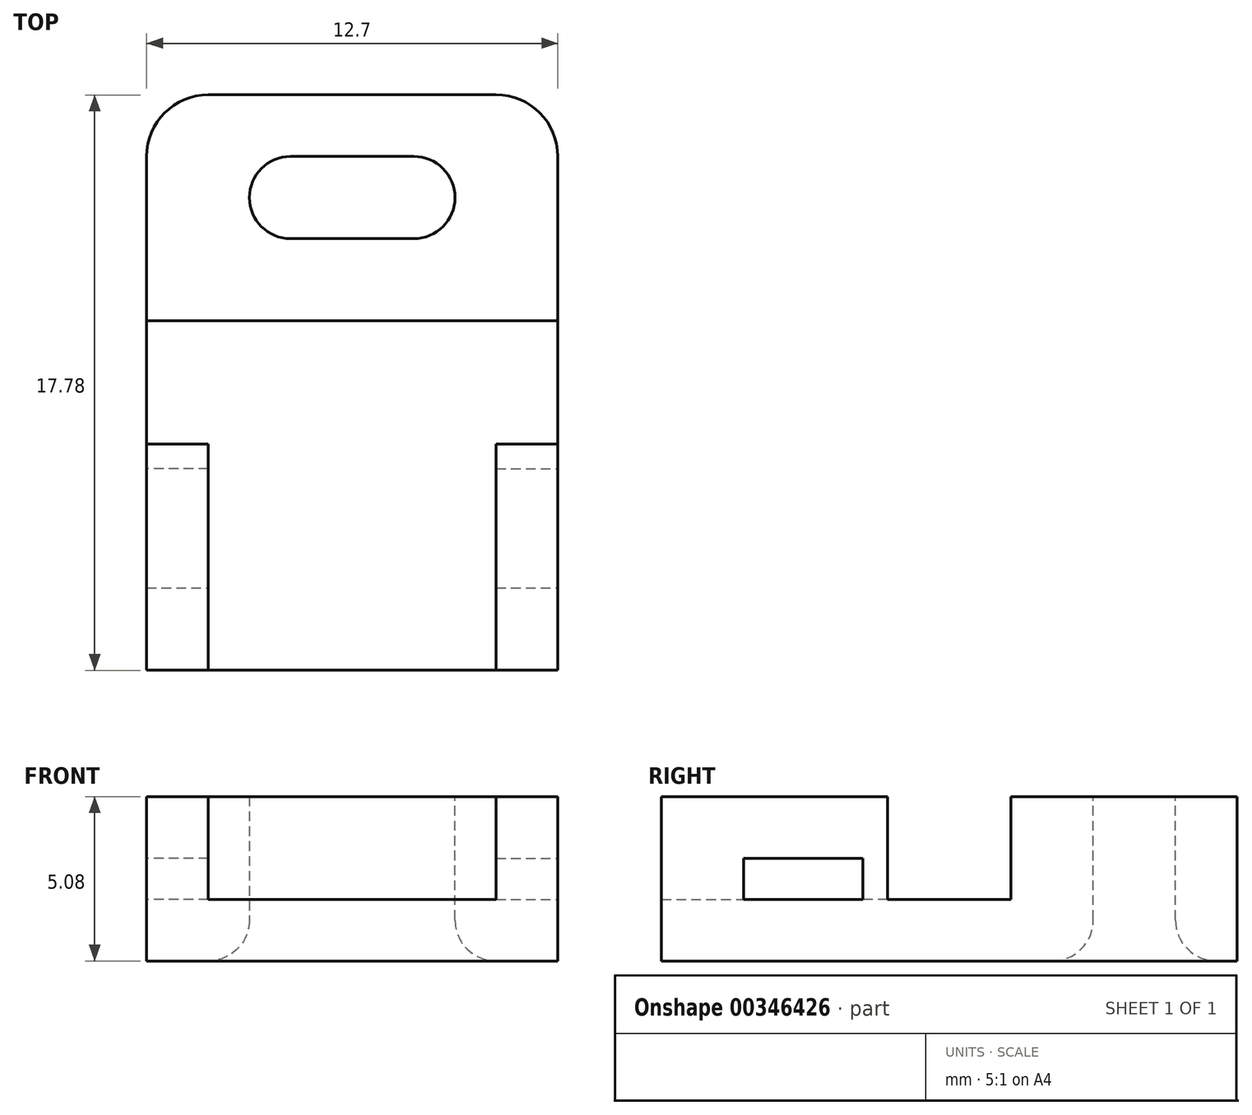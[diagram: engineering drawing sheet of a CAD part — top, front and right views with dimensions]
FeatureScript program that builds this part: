
annotation { "Feature Type Name" : "Feature", "Feature Type Description" : "" }
export const myFeature = defineFeature(function(context is Context, id is Id, definition is map)
    precondition{}
    {
        {
            var Q0;
            Q0=qCreatedBy(makeId("Top.planeOp"),FACE);
            var sketch = newSketch(context, id + "F0", { "sketchPlane" : qUnion([Q0])});
            skLineSegment(sketch, "E0.bottom", {"start": v(-27.07, 22.58) * mm, "end": v(-14.37, 22.58) * mm});
            skLineSegment(sketch, "E0.top", {"start": v(-27.07, 7.34) * mm, "end": v(-14.37, 7.34) * mm});
            skLineSegment(sketch, "E0.left", {"start": v(-27.07, 22.58) * mm, "end": v(-27.07, 7.34) * mm});
            skLineSegment(sketch, "E0.right", {"start": v(-14.37, 22.58) * mm, "end": v(-14.37, 7.34) * mm});
            skSolve(sketch);
        }
        {
            var Q0;
            Q0=makeQuery(id+"F0.imprint","IMPRINT",FACE,{"disambiguationData":[TD([[makeQuery(id+"F0.imprint","IMPRINT",EDGE,{"derivedFrom":sQuery(id+"F0.wireOp",EDGE,"E0.bottom")}),-1.0]])]});
            extrude(context, id + "F1", {"entities" : qUnion([Q0]), "depth" : 5.08 * mm});
        }
        {
            var Q0;
            Q0=makeQuery(id+"F1.opExtrude","CAP_FACE",FACE,{"disambiguationData":[OSD([sQuery(id+"F0.wireOp",EDGE,"E0.bottom"),sQuery(id+"F0.wireOp",EDGE,"E0.top"),sQuery(id+"F0.wireOp",EDGE,"E0.left"),sQuery(id+"F0.wireOp",EDGE,"E0.right")])],"isStart":false});
            var sketch = newSketch(context, id + "F2", { "sketchPlane" : qUnion([Q0])});
            skLineSegment(sketch, "E1.bottom", {"start": v(-23.9, 20.68) * mm, "end": v(-17.55, 20.68) * mm});
            skLineSegment(sketch, "E1.top", {"start": v(-23.9, 18.14) * mm, "end": v(-17.55, 18.14) * mm});
            skLineSegment(sketch, "E1.left", {"start": v(-23.9, 20.68) * mm, "end": v(-23.9, 18.14) * mm});
            skLineSegment(sketch, "E1.right", {"start": v(-17.55, 20.68) * mm, "end": v(-17.55, 18.14) * mm});
            skPoint(sketch, "E1.middle", {"position": v(-20.72, 19.4) * mm});
            skPoint(sketch, "E1.middle.positionSnap0", {"position": v(-20.72, 22.58) * mm});
            skPoint(sketch, "E1.centerSnap0", {"position": v(-20.72, 22.58) * mm});
            skSolve(sketch);
        }
        {
            var Q0;
            Q0=makeQuery(id+"F2.imprint","IMPRINT",FACE,{"disambiguationData":[TD([[makeQuery(id+"F2.imprint","IMPRINT",EDGE,{"derivedFrom":sQuery(id+"F2.wireOp",EDGE,"E1.bottom")}),-1.0]])]});
            extrude(context, id + "F3", {"entities" : qUnion([Q0]), "operationType" : NewBodyOperationType.REMOVE, "oppositeDirection" : true, "depth" : 25.4 * mm});
        }
        {
            var Q0;
            Q0=makeQuery(id+"F3.boolean.opBoolean","COPY",EDGE,{"derivedFrom":makeQuery(id+"F3.opExtrude","CAP_EDGE",EDGE,{"disambiguationData":[OSD([sQuery(id+"F2.wireOp",EDGE,"E1.top")])],"isStart":true})});
            var Q1;
            Q1=makeQuery(id+"F3.boolean.opBoolean","COPY",EDGE,{"derivedFrom":makeQuery(id+"F3.opExtrude","CAP_EDGE",EDGE,{"disambiguationData":[OSD([sQuery(id+"F2.wireOp",EDGE,"E1.right")])],"isStart":true})});
            var Q2;
            Q2=makeQuery(id+"F3.boolean.opBoolean","COPY",EDGE,{"derivedFrom":makeQuery(id+"F3.opExtrude","CAP_EDGE",EDGE,{"disambiguationData":[OSD([sQuery(id+"F2.wireOp",EDGE,"E1.left")])],"isStart":true})});
            var Q3;
            Q3=makeQuery(id+"F3.boolean.opBoolean","COPY",EDGE,{"derivedFrom":makeQuery(id+"F3.opExtrude","CAP_EDGE",EDGE,{"disambiguationData":[OSD([sQuery(id+"F2.wireOp",EDGE,"E1.bottom")])],"isStart":true})});
            var Q4;
            Q4=makeQuery(id+"F3.boolean.opBoolean","INTERSECT",EDGE,{"derivedFrom":[makeQuery(id+"F1.opExtrude","CAP_FACE",FACE,{"disambiguationData":[OSD([sQuery(id+"F0.wireOp",EDGE,"E0.bottom"),sQuery(id+"F0.wireOp",EDGE,"E0.top"),sQuery(id+"F0.wireOp",EDGE,"E0.left"),sQuery(id+"F0.wireOp",EDGE,"E0.right")])],"isStart":true}),makeQuery(id+"F3.opExtrude","SWEPT_FACE",FACE,{"disambiguationData":[OSD([sQuery(id+"F2.wireOp",EDGE,"E1.right")])]})]});
            var Q5;
            Q5=makeQuery(id+"F3.boolean.opBoolean","INTERSECT",EDGE,{"derivedFrom":[makeQuery(id+"F1.opExtrude","CAP_FACE",FACE,{"disambiguationData":[OSD([sQuery(id+"F0.wireOp",EDGE,"E0.bottom"),sQuery(id+"F0.wireOp",EDGE,"E0.top"),sQuery(id+"F0.wireOp",EDGE,"E0.left"),sQuery(id+"F0.wireOp",EDGE,"E0.right")])],"isStart":true}),makeQuery(id+"F3.opExtrude","SWEPT_FACE",FACE,{"disambiguationData":[OSD([sQuery(id+"F2.wireOp",EDGE,"E1.top")])]})]});
            var Q6;
            Q6=makeQuery(id+"F3.boolean.opBoolean","INTERSECT",EDGE,{"derivedFrom":[makeQuery(id+"F1.opExtrude","CAP_FACE",FACE,{"disambiguationData":[OSD([sQuery(id+"F0.wireOp",EDGE,"E0.bottom"),sQuery(id+"F0.wireOp",EDGE,"E0.top"),sQuery(id+"F0.wireOp",EDGE,"E0.left"),sQuery(id+"F0.wireOp",EDGE,"E0.right")])],"isStart":true}),makeQuery(id+"F3.opExtrude","SWEPT_FACE",FACE,{"disambiguationData":[OSD([sQuery(id+"F2.wireOp",EDGE,"E1.left")])]})]});
            var Q7;
            Q7=makeQuery(id+"F3.boolean.opBoolean","INTERSECT",EDGE,{"derivedFrom":[makeQuery(id+"F1.opExtrude","CAP_FACE",FACE,{"disambiguationData":[OSD([sQuery(id+"F0.wireOp",EDGE,"E0.bottom"),sQuery(id+"F0.wireOp",EDGE,"E0.top"),sQuery(id+"F0.wireOp",EDGE,"E0.left"),sQuery(id+"F0.wireOp",EDGE,"E0.right")])],"isStart":true}),makeQuery(id+"F3.opExtrude","SWEPT_FACE",FACE,{"disambiguationData":[OSD([sQuery(id+"F2.wireOp",EDGE,"E1.bottom")])]})]});
            var Q8;
            Q8=makeQuery(id+"F3.boolean.opBoolean","COPY",EDGE,{"derivedFrom":makeQuery(id+"F3.opExtrude","SWEPT_EDGE",EDGE,{"disambiguationData":[OSD([sQuery(id+"F2.wireOp",EDGE,"E1.top"),sQuery(id+"F2.wireOp",EDGE,"E1.right")])]})});
            var Q9;
            Q9=makeQuery(id+"F3.boolean.opBoolean","COPY",EDGE,{"derivedFrom":makeQuery(id+"F3.opExtrude","SWEPT_EDGE",EDGE,{"disambiguationData":[OSD([sQuery(id+"F2.wireOp",EDGE,"E1.top"),sQuery(id+"F2.wireOp",EDGE,"E1.left")])]})});
            var Q10;
            Q10=makeQuery(id+"F3.boolean.opBoolean","COPY",EDGE,{"derivedFrom":makeQuery(id+"F3.opExtrude","SWEPT_EDGE",EDGE,{"disambiguationData":[OSD([sQuery(id+"F2.wireOp",EDGE,"E1.bottom"),sQuery(id+"F2.wireOp",EDGE,"E1.left")])]})});
            var Q11;
            Q11=makeQuery(id+"F3.boolean.opBoolean","COPY",EDGE,{"derivedFrom":makeQuery(id+"F3.opExtrude","SWEPT_EDGE",EDGE,{"disambiguationData":[OSD([sQuery(id+"F2.wireOp",EDGE,"E1.bottom"),sQuery(id+"F2.wireOp",EDGE,"E1.right")])]})});
            fillet(context, id + "F4", {"entities" : qUnion([Q0, Q1, Q2, Q3, Q4, Q5, Q6, Q7, Q8, Q9, Q10, Q11]), "radius" : 1.27 * mm, "tangentPropagation" : true, "allowEdgeOverflow" : false});
        }
        {
            var Q0;
            Q0=makeQuery(id+"F1.opExtrude","SWEPT_EDGE",EDGE,{"disambiguationData":[OSD([sQuery(id+"F0.wireOp",EDGE,"E0.bottom"),sQuery(id+"F0.wireOp",EDGE,"E0.left")])]});
            var Q1;
            Q1=makeQuery(id+"F1.opExtrude","SWEPT_EDGE",EDGE,{"disambiguationData":[OSD([sQuery(id+"F0.wireOp",EDGE,"E0.bottom"),sQuery(id+"F0.wireOp",EDGE,"E0.right")])]});
            fillet(context, id + "F5", {"entities" : qUnion([Q0, Q1]), "radius" : 1.9 * mm, "tangentPropagation" : true, "allowEdgeOverflow" : false});
        }
        {
            var Q0;
            Q0=makeQuery(id+"F1.opExtrude","SWEPT_FACE",FACE,{"disambiguationData":[OSD([sQuery(id+"F0.wireOp",EDGE,"E0.right")])]});
            var sketch = newSketch(context, id + "F6", { "sketchPlane" : qUnion([Q0])});
            skLineSegment(sketch, "E2.bottom", {"start": v(9.88, 3.17) * mm, "end": v(15.6, 3.17) * mm});
            skLineSegment(sketch, "E2.top", {"start": v(9.88, 1.9) * mm, "end": v(15.6, 1.9) * mm});
            skLineSegment(sketch, "E2.left", {"start": v(9.88, 3.17) * mm, "end": v(9.88, 1.9) * mm});
            skLineSegment(sketch, "E2.right", {"start": v(15.6, 3.17) * mm, "end": v(15.6, 1.9) * mm});
            skPoint(sketch, "E2.middle", {"position": v(12.74, 2.54) * mm});
            skPoint(sketch, "E2.middle.positionSnap0", {"position": v(7.34, 2.54) * mm});
            skPoint(sketch, "E2.centerSnap0", {"position": v(7.34, 2.54) * mm});
            skSolve(sketch);
        }
        {
            var Q0;
            Q0 = qSketchRegion(id + "F6", true);
            extrude(context, id + "F7", {"entities" : qUnion([Q0]), "operationType" : NewBodyOperationType.REMOVE, "oppositeDirection" : true, "depth" : 25.4 * mm});
        }
        {
            var Q0;
            Q0=makeQuery(id+"F1.opExtrude","CAP_FACE",FACE,{"disambiguationData":[OSD([sQuery(id+"F0.wireOp",EDGE,"E0.bottom"),sQuery(id+"F0.wireOp",EDGE,"E0.top"),sQuery(id+"F0.wireOp",EDGE,"E0.left"),sQuery(id+"F0.wireOp",EDGE,"E0.right")])],"isStart":false});
            var sketch = newSketch(context, id + "F8", { "sketchPlane" : qUnion([Q0])});
            skLineSegment(sketch, "E3.bottom", {"start": v(-25.17, 7.34) * mm, "end": v(-16.28, 7.34) * mm});
            skLineSegment(sketch, "E3.top", {"start": v(-25.17, 15.6) * mm, "end": v(-16.28, 15.6) * mm});
            skLineSegment(sketch, "E3.left", {"start": v(-25.17, 7.34) * mm, "end": v(-25.17, 15.6) * mm});
            skLineSegment(sketch, "E3.right", {"start": v(-16.28, 7.34) * mm, "end": v(-16.28, 15.6) * mm});
            skPoint(sketch, "E3.middle", {"position": v(-20.72, 11.47) * mm});
            skPoint(sketch, "E3.middle.positionSnap0", {"position": v(-20.72, 7.34) * mm});
            skPoint(sketch, "E3.centerSnap0", {"position": v(-20.72, 7.34) * mm});
            skSolve(sketch);
        }
        {
            var Q0;
            Q0 = qSketchRegion(id + "F8", true);
            var Q1;
            Q1=makeQuery(id+"F7.boolean.opBoolean","COPY",FACE,{"derivedFrom":makeQuery(id+"F7.opExtrude","SWEPT_FACE",FACE,{"disambiguationData":[OSD([sQuery(id+"F6.wireOp",EDGE,"E2.top")])]})});
            extrude(context, id + "F9", {"entities" : qUnion([Q0]), "operationType" : NewBodyOperationType.REMOVE, "endBound" : BoundingType.UP_TO_SURFACE, "oppositeDirection" : true, "endBoundEntityFace" : qUnion([Q1]), "depth" : 25.4 * mm});
        }
        {
            var Q0;
            Q0=makeQuery(id+"F1.opExtrude","CAP_FACE",FACE,{"disambiguationData":[OSD([sQuery(id+"F0.wireOp",EDGE,"E0.bottom"),sQuery(id+"F0.wireOp",EDGE,"E0.top"),sQuery(id+"F0.wireOp",EDGE,"E0.left"),sQuery(id+"F0.wireOp",EDGE,"E0.right")])],"isStart":false});
            var sketch = newSketch(context, id + "F10", { "sketchPlane" : qUnion([Q0])});
            skLineSegment(sketch, "E4.bottom", {"start": v(-14.37, 15.6) * mm, "end": v(-27.07, 15.6) * mm});
            skLineSegment(sketch, "E4.top", {"start": v(-14.37, 11.79) * mm, "end": v(-27.07, 11.79) * mm});
            skLineSegment(sketch, "E4.left", {"start": v(-14.37, 15.6) * mm, "end": v(-14.37, 11.79) * mm});
            skLineSegment(sketch, "E4.right", {"start": v(-27.07, 15.6) * mm, "end": v(-27.07, 11.79) * mm});
            skSolve(sketch);
        }
        {
            var Q0;
            {var subQ3=sQuery(id+"F10.wireOp",EDGE,"E4.right");Q0=makeQuery(id+"F10.imprint","IMPRINT",FACE,{"disambiguationData":[TD([[makeQuery(id+"F10.imprint","IMPRINT",EDGE,{"derivedFrom":subQ3}),1.0]])]});}
            var Q1;
            {var subQ3=sQuery(id+"F10.wireOp",EDGE,"E4.left");Q1=makeQuery(id+"F10.imprint","IMPRINT",FACE,{"disambiguationData":[TD([[makeQuery(id+"F10.imprint","IMPRINT",EDGE,{"derivedFrom":subQ3}),-1.0]])]});}
            extrude(context, id + "F11", {"entities" : qUnion([Q0, Q1]), "operationType" : NewBodyOperationType.REMOVE, "endBound" : BoundingType.UP_TO_NEXT, "oppositeDirection" : true, "depth" : 25.4 * mm});
        }
        {
            var Q0;
            Q0=makeQuery(id+"F1.opExtrude","SWEPT_FACE",FACE,{"disambiguationData":[OSD([sQuery(id+"F0.wireOp",EDGE,"E0.top")])]});
            extrude(context, id + "F12", {"entities" : qUnion([Q0]), "operationType" : NewBodyOperationType.ADD, "depth" : 2.54 * mm});
        }
        {
            var Q0;
            {var subQ0=sQuery(id+"F0.wireOp",EDGE,"E0.right");Q0=makeQuery(id+"F12.boolean.opBoolean","MERGE",FACE,{"derivedFrom":[makeQuery(id+"F1.opExtrude","SWEPT_FACE",FACE,{"disambiguationData":[OSD([subQ0])]}),makeQuery(id+"F12.opExtrude","SWEPT_FACE",FACE,{"disambiguationData":[OSD([sQuery(id+"F0.wireOp",EDGE,"E0.top"),subQ0])]})]});}
            var sketch = newSketch(context, id + "F13", { "sketchPlane" : qUnion([Q0])});
            skLineSegment(sketch, "E5.bottom", {"start": v(9.88, 3.17) * mm, "end": v(7.34, 3.17) * mm});
            skLineSegment(sketch, "E5.top", {"start": v(9.88, 1.9) * mm, "end": v(7.34, 1.9) * mm});
            skLineSegment(sketch, "E5.left", {"start": v(9.88, 3.17) * mm, "end": v(9.88, 1.9) * mm});
            skLineSegment(sketch, "E5.right", {"start": v(7.34, 3.17) * mm, "end": v(7.34, 1.9) * mm});
            skSolve(sketch);
        }
        {
            var Q0;
            Q0 = qSketchRegion(id + "F13", true);
            extrude(context, id + "F14", {"entities" : qUnion([Q0]), "operationType" : NewBodyOperationType.REMOVE, "oppositeDirection" : true, "depth" : 25.4 * mm});
        }
        {
            var Q0;
            Q0=makeQuery(id+"F14.boolean.opBoolean","MERGE",FACE,{"derivedFrom":[makeQuery(id+"F9.boolean.opBoolean","SPLIT",FACE,{"disambiguationData":[TD([makeQuery(id+"F1.opExtrude","SWEPT_FACE",FACE,{"disambiguationData":[OSD([sQuery(id+"F0.wireOp",EDGE,"E0.right")])]})])],"derivedFrom":makeQuery(id+"F7.boolean.opBoolean","COPY",FACE,{"derivedFrom":makeQuery(id+"F7.opExtrude","SWEPT_FACE",FACE,{"disambiguationData":[OSD([sQuery(id+"F6.wireOp",EDGE,"E2.bottom")])]})})})],"fromTools":[makeQuery(id+"F14.opExtrude","SWEPT_FACE",FACE,{"disambiguationData":[OSD([sQuery(id+"F13.wireOp",EDGE,"E5.bottom")])]})]});
            var sketch = newSketch(context, id + "F15", { "sketchPlane" : qUnion([Q0])});
            skLineSegment(sketch, "E6.bottom", {"start": v(-16.28, -11.79) * mm, "end": v(-14.37, -11.79) * mm});
            skLineSegment(sketch, "E6.top", {"start": v(-16.28, -11.03) * mm, "end": v(-14.37, -11.03) * mm});
            skLineSegment(sketch, "E6.left", {"start": v(-16.28, -11.79) * mm, "end": v(-16.28, -11.03) * mm});
            skLineSegment(sketch, "E6.right", {"start": v(-14.37, -11.79) * mm, "end": v(-14.37, -11.03) * mm});
            skSolve(sketch);
        }
        {
            var Q0;
            Q0 = qSketchRegion(id + "F15", true);
            extrude(context, id + "F16", {"entities" : qUnion([Q0]), "operationType" : NewBodyOperationType.ADD, "endBound" : BoundingType.UP_TO_NEXT, "depth" : 25.4 * mm});
        }
        {
            var Q0;
            Q0=makeQuery(id+"F14.boolean.opBoolean","MERGE",FACE,{"derivedFrom":[makeQuery(id+"F9.boolean.opBoolean","SPLIT",FACE,{"disambiguationData":[TD([makeQuery(id+"F1.opExtrude","SWEPT_FACE",FACE,{"disambiguationData":[OSD([sQuery(id+"F0.wireOp",EDGE,"E0.left")])]})])],"derivedFrom":makeQuery(id+"F7.boolean.opBoolean","COPY",FACE,{"derivedFrom":makeQuery(id+"F7.opExtrude","SWEPT_FACE",FACE,{"disambiguationData":[OSD([sQuery(id+"F6.wireOp",EDGE,"E2.bottom")])]})})})],"fromTools":[makeQuery(id+"F14.opExtrude","SWEPT_FACE",FACE,{"disambiguationData":[OSD([sQuery(id+"F13.wireOp",EDGE,"E5.bottom")])]})]});
            var sketch = newSketch(context, id + "F17", { "sketchPlane" : qUnion([Q0])});
            skLineSegment(sketch, "E7.bottom", {"start": v(-25.17, -11.79) * mm, "end": v(-27.07, -11.79) * mm});
            skLineSegment(sketch, "E7.top", {"start": v(-25.17, -11.03) * mm, "end": v(-27.07, -11.03) * mm});
            skLineSegment(sketch, "E7.left", {"start": v(-25.17, -11.79) * mm, "end": v(-25.17, -11.03) * mm});
            skLineSegment(sketch, "E7.right", {"start": v(-27.07, -11.79) * mm, "end": v(-27.07, -11.03) * mm});
            skSolve(sketch);
        }
        {
            var Q0;
            Q0 = qSketchRegion(id + "F17", true);
            extrude(context, id + "F18", {"entities" : qUnion([Q0]), "operationType" : NewBodyOperationType.ADD, "endBound" : BoundingType.UP_TO_NEXT, "depth" : 25.4 * mm});
        }
    });
